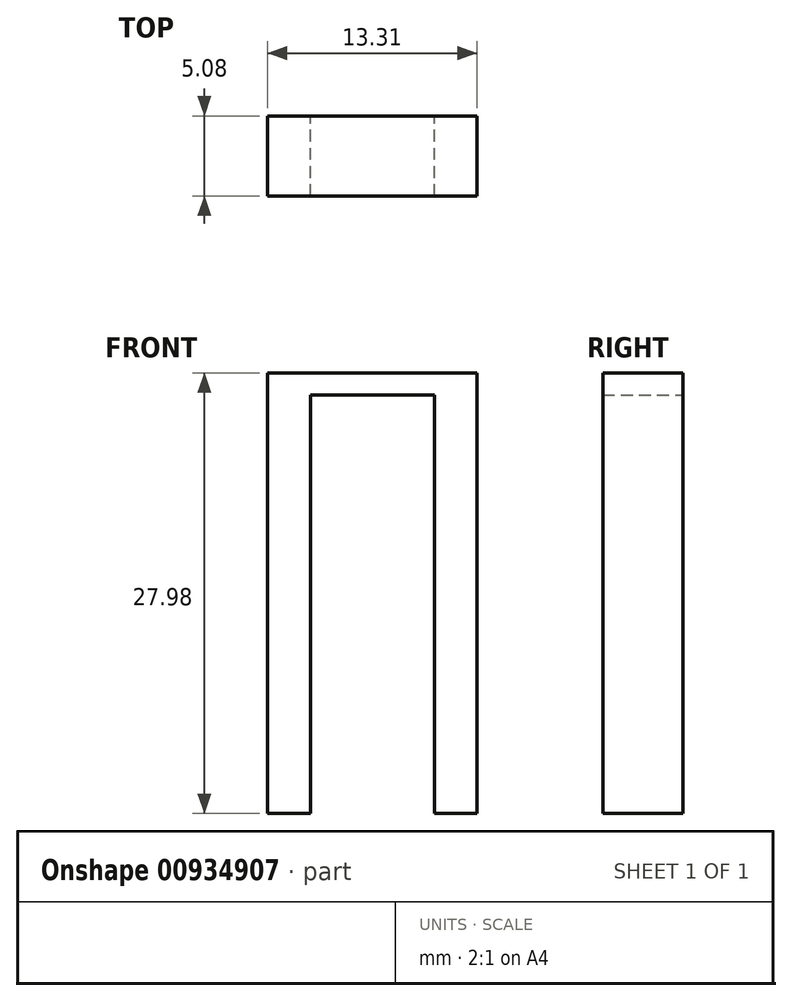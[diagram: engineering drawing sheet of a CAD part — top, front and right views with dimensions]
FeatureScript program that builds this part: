
annotation { "Feature Type Name" : "Feature", "Feature Type Description" : "" }
export const myFeature = defineFeature(function(context is Context, id is Id, definition is map)
    precondition{}
    {
        {
            var Q0;
            Q0=qCreatedBy(makeId("Front.planeOp"),FACE);
            var sketch = newSketch(context, id + "F0", { "sketchPlane" : qUnion([Q0])});
            skLineSegment(sketch, "E0.bottom", {"start": v(-10.57, 0) * mm, "end": v(-2.7, 0) * mm});
            skLineSegment(sketch, "E0.top", {"start": v(-10.57, 1.38) * mm, "end": v(-2.7, 1.38) * mm});
            skLineSegment(sketch, "E0.left", {"start": v(-10.57, 0) * mm, "end": v(-10.57, 1.38) * mm});
            skLineSegment(sketch, "E0.right", {"start": v(-2.7, 0) * mm, "end": v(-2.7, 1.38) * mm});
            skLineSegment(sketch, "E1.bottom", {"start": v(-10.57, 1.38) * mm, "end": v(-13.3, 1.38) * mm});
            skLineSegment(sketch, "E1.top", {"start": v(-10.57, -26.6) * mm, "end": v(-13.3, -26.6) * mm});
            skLineSegment(sketch, "E1.left", {"start": v(-10.57, 1.38) * mm, "end": v(-10.57, -26.6) * mm});
            skLineSegment(sketch, "E1.right", {"start": v(-13.3, 1.38) * mm, "end": v(-13.3, -26.6) * mm});
            skLineSegment(sketch, "E2.bottom", {"start": v(-2.7, 1.38) * mm, "end": v(0, 1.38) * mm});
            skLineSegment(sketch, "E2.top", {"start": v(-2.7, -26.6) * mm, "end": v(0, -26.6) * mm});
            skLineSegment(sketch, "E2.left", {"start": v(-2.7, 1.38) * mm, "end": v(-2.7, -26.6) * mm});
            skLineSegment(sketch, "E2.right", {"start": v(0, 1.38) * mm, "end": v(0, -26.6) * mm});
            skSolve(sketch);
        }
        {
            var Q0;
            {var subQ3=sQuery(id+"F0.wireOp",EDGE,"E1.bottom");Q0=makeQuery(id+"F0.imprint","IMPRINT",FACE,{"disambiguationData":[TD([[makeQuery(id+"F0.imprint","IMPRINT",EDGE,{"derivedFrom":subQ3}),1.0]])]});}
            var Q1;
            {var subQ0=sQuery(id+"F0.wireOp",EDGE,"E0.bottom");Q1=makeQuery(id+"F0.imprint","IMPRINT",FACE,{"disambiguationData":[TD([[makeQuery(id+"F0.imprint","IMPRINT",EDGE,{"derivedFrom":subQ0}),1.0]])]});}
            var Q2;
            {var subQ3=sQuery(id+"F0.wireOp",EDGE,"E2.bottom");Q2=makeQuery(id+"F0.imprint","IMPRINT",FACE,{"disambiguationData":[TD([[makeQuery(id+"F0.imprint","IMPRINT",EDGE,{"derivedFrom":subQ3}),-1.0]])]});}
            extrude(context, id + "F1", {"entities" : qUnion([Q0, Q1, Q2]), "depth" : 5.08 * mm, "offsetDistance" : 25.4 * mm});
        }
    });
